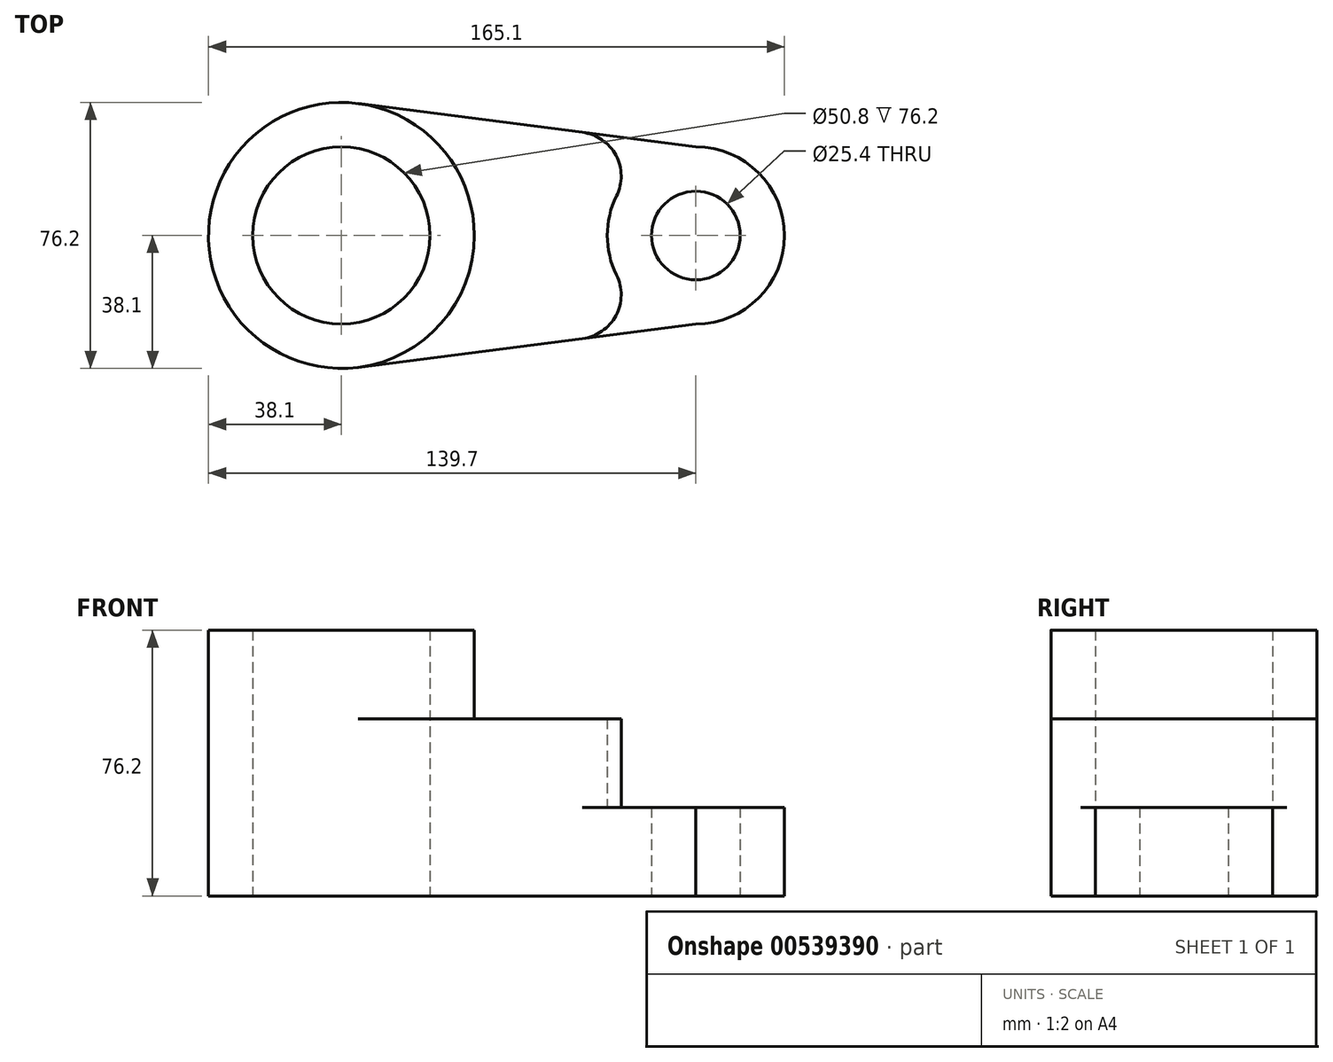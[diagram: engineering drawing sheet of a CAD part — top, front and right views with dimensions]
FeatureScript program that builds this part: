
annotation { "Feature Type Name" : "Feature", "Feature Type Description" : "" }
export const myFeature = defineFeature(function(context is Context, id is Id, definition is map)
    precondition{}
    {
        {
            var Q0;
            Q0=qCreatedBy(makeId("Top.planeOp"),FACE);
            var sketch = newSketch(context, id + "F0", { "sketchPlane" : qUnion([Q0])});
            skCircle(sketch, "E0", {"center": v(0, 0) * mm, "radius": 25.4 * mm});
            skCircle(sketch, "E1", {"center": v(101.6, 0) * mm, "radius": 12.7 * mm});
            skCircle(sketch, "E2", {"center": v(0, 0) * mm, "radius": 38.1 * mm});
            skCircle(sketch, "E3", {"center": v(101.6, 0) * mm, "radius": 25.4 * mm});
            skLineSegment(sketch, "E4", {"start": v(101.6, 25.4) * mm, "end": v(4.84, 37.8) * mm});
            skLineSegment(sketch, "E5", {"start": v(4.84, -37.8) * mm, "end": v(101.6, -25.4) * mm});
            skSolve(sketch);
        }
        {
            var Q0;
            Q0=makeQuery(id+"F0.imprint","IMPRINT",FACE,{"disambiguationData":[TD([[makeQuery(id+"F0.imprint","IMPRINT",EDGE,{"derivedFrom":sQuery(id+"F0.wireOp",EDGE,"E0")}),-1.0]])]});
            var Q1;
            {var subQ0=sQuery(id+"F0.wireOp",EDGE,"H58HY6Zb-zd0C-wShN-Wv4e-E45ocX78umRN");var subQ1=sQuery(id+"F0.wireOp",EDGE,"E2");var subQ2=makeQuery(id+"F0.imprint","INTERSECT",VERTEX,{"disambiguationData":[OD(1.0)],"derivedFrom":[subQ1,subQ0]});Q1=makeQuery(id+"F0.imprint","IMPRINT",FACE,{"disambiguationData":[TD([[makeQuery(id+"F0.imprint","IMPRINT",EDGE,{"disambiguationData":[TD([[subQ2,1.0]])],"derivedFrom":subQ1}),-1.0]])]});}
            var Q2;
            Q2=makeQuery(id+"F0.imprint","IMPRINT",FACE,{"disambiguationData":[TD([[makeQuery(id+"F0.imprint","IMPRINT",EDGE,{"derivedFrom":sQuery(id+"F0.wireOp",EDGE,"E1")}),-1.0]])]});
            extrude(context, id + "F1", {"entities" : qUnion([Q0, Q1, Q2]), "depth" : 25.4 * mm, "offsetDistance" : 25.4 * mm});
        }
        {
            var Q0;
            Q0=makeQuery(id+"F0.imprint","IMPRINT",FACE,{"disambiguationData":[TD([[makeQuery(id+"F0.imprint","IMPRINT",EDGE,{"derivedFrom":sQuery(id+"F0.wireOp",EDGE,"E0")}),-1.0]])]});
            var Q1;
            {var subQ0=sQuery(id+"F0.wireOp",EDGE,"E4");Q1=makeQuery(id+"F0.imprint","IMPRINT",FACE,{"disambiguationData":[TD([[makeQuery(id+"F0.imprint","IMPRINT",EDGE,{"derivedFrom":subQ0}),1.0]])]});}
            extrude(context, id + "F2", {"entities" : qUnion([Q0, Q1]), "operationType" : NewBodyOperationType.ADD, "depth" : 50.8 * mm, "offsetDistance" : 25.4 * mm});
        }
        {
            var Q0;
            Q0=makeQuery(id+"F0.imprint","IMPRINT",FACE,{"disambiguationData":[TD([[makeQuery(id+"F0.imprint","IMPRINT",EDGE,{"derivedFrom":sQuery(id+"F0.wireOp",EDGE,"E0")}),-1.0]])]});
            extrude(context, id + "F3", {"entities" : qUnion([Q0]), "operationType" : NewBodyOperationType.ADD, "depth" : 76.2 * mm, "offsetDistance" : 25.4 * mm});
        }
        {
            var Q0;
            Q0=makeQuery(id+"F2.opExtrude","SWEPT_EDGE",EDGE,{"disambiguationData":[OSD([sQuery(id+"F0.wireOp",EDGE,"E3"),sQuery(id+"F0.wireOp",EDGE,"E5")])]});
            var Q1;
            Q1=makeQuery(id+"F2.opExtrude","SWEPT_EDGE",EDGE,{"disambiguationData":[OSD([sQuery(id+"F0.wireOp",EDGE,"E3"),sQuery(id+"F0.wireOp",EDGE,"E4")])]});
            fillet(context, id + "F4", {"entities" : qUnion([Q0, Q1]), "radius" : 12.7 * mm, "tangentPropagation" : true, "allowEdgeOverflow" : false});
        }
    });
